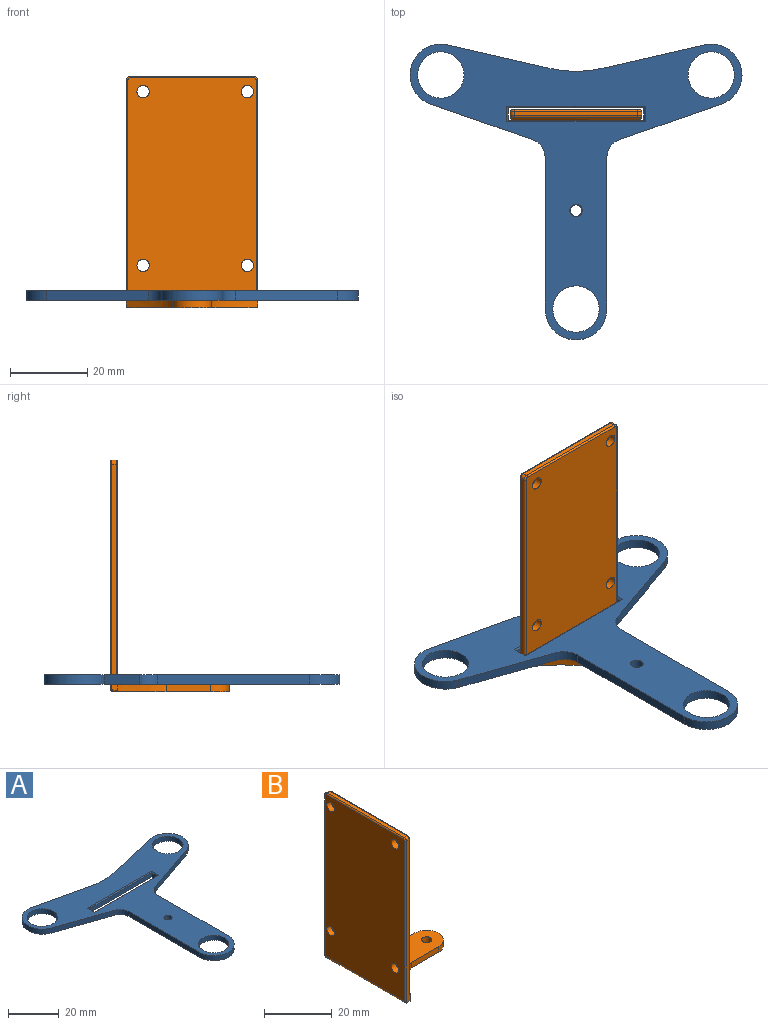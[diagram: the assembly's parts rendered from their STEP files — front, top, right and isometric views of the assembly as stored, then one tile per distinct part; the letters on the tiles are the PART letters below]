
ASSEMBLY  parts=2 mates=1
PART A: 26 faces, bbox 86x76.6x2.4 mm
  f0: plane 26.46x6.1mm, normal (0.22,0.97,0), area 65.2mm2, adj f1,f17,f18,f23
  f1: cylinder r=8mm len=15.55mm, axis (0,0,-1), area 58.2mm2, adj f0,f2,f17,f18
  f2: plane 26.29x9.18mm, normal (-0.33,-0.94,0), area 66.8mm2, adj f1,f17,f18,f24
  f3: plane 39.17x2.4mm, normal (-1,0,0), area 94mm2, adj f4,f17,f18,f24
  f4: cylinder r=8mm len=16mm, axis (0,0,-1), area 60.3mm2, adj f3,f5,f17,f18
  f5: plane 39.17x2.4mm, normal (1,0,0), area 94mm2, adj f4,f17,f18,f25
  f6: plane 26.29x9.18mm, normal (0.33,-0.94,0), area 66.8mm2, adj f7,f17,f18,f25
  f7: cylinder r=8mm len=15.55mm, axis (0,0,-1), area 58.2mm2, adj f6,f16,f17,f18
  f8: plane 3.2x2mm, normal (-1,0,0), area 6.4mm2, adj f9,f15,f18,f22
  f9: plane 35x2mm, normal (0,1,0), area 70mm2, adj f8,f10,f18,f20
  f10: plane 3.2x2mm, normal (1,0,0), area 6.4mm2, adj f9,f15,f18,f19
  f11: cylinder r=6mm len=12mm, axis (0,0,-1), area 90.5mm2, adj f17,f18
  f12: cylinder r=6mm len=12mm, axis (0,0,-1), area 90.5mm2, adj f17,f18
  f13: cylinder r=6mm len=12mm, axis (0,0,-1), area 90.5mm2, adj f17,f18
  f14: cylinder r=1.6mm len=3.2mm, axis (0,0,-1), area 24.1mm2, adj f17,f18
  f15: plane 35x2mm, normal (0,-1,0), area 70mm2, adj f8,f10,f18,f21
  f16: plane 26.47x6.1mm, normal (-0.22,0.97,0), area 65.2mm2, adj f7,f17,f18,f23
  f17: plane 86x76.62mm, normal (0,0,1), area 1794.3mm2, adj f0,f1,f2,f3,f4,f5,f6,f7
  f18: plane 86x76.62mm, normal (0,0,-1), area 1825.5mm2, adj f0,f1,f2,f3,f4,f5,f6,f7
  f19: plane 4x0.4mm, normal (0.71,0,0.71), area 2mm2, adj f10,f17,f20,f21
  f20: plane 35.8x0.4mm, normal (0,0.71,0.71), area 20mm2, adj f9,f17,f19,f22
  f21: plane 35.8x0.4mm, normal (0,-0.71,0.71), area 20mm2, adj f15,f17,f19,f22
  f22: plane 4x0.4mm, normal (-0.71,0,0.71), area 2mm2, adj f8,f17,f20,f21
  f23: cylinder r=30mm len=13.48mm, axis (0,0,-1), area 32.6mm2, adj f0,f16,f17,f18
  f24: cylinder r=5mm len=4.72mm, axis (0,0,1), area 14.8mm2, adj f2,f3,f17,f18
  f25: cylinder r=5mm len=4.72mm, axis (0,0,1), area 14.8mm2, adj f5,f6,f17,f18
PART B: 37 faces, bbox 30.9x34.2x60.2 mm
  f0: plane 58.6x1.6mm, normal (0,-1,0), area 71.2mm2, adj f1,f18,f21,f22,f23,f31,f33
  f1: extruded ~12.5x12mm, area 35.7mm2, adj f0,f2,f9,f10,f17,f21,f31
  f2: plane 11.5x2mm, normal (0,-1,0), area 23mm2, adj f1,f3,f9,f10
  f3: cylinder r=5mm len=10mm, axis (0,0,-1), area 30.6mm2, adj f2,f4,f9,f10
  f4: plane 12x2mm, normal (0,1,0), area 24mm2, adj f3,f5,f9,f10
  f5: extruded ~12x12mm, area 35.1mm2, adj f4,f6,f9,f10,f17,f29,f30
  f6: plane 58.6x1.6mm, normal (0,1,0), area 71.2mm2, adj f5,f19,f27,f28,f29,f30,f32
  f7: plane 58.6x33.2mm, normal (-1,0,0), area 1913.2mm2, adj f13,f14,f15,f16,f20,f23,f24,f25
  f8: cylinder r=1.5mm len=3mm, axis (0,0,-1), area 18.8mm2, adj f9,f10
  f9: plane 30.38x27.47mm, normal (0,0,1), area 342.9mm2, adj f1,f2,f3,f4,f5,f8,f17
  f10: plane 33.86x29.8mm, normal (0,0,-1), area 427.1mm2, adj f1,f2,f3,f4,f5,f8,f20,f21
  f11: plane 56x33.2mm, normal (1,0,0), area 1826.9mm2, adj f13,f14,f15,f16,f17,f32,f33,f34
  f12: plane 32x1.2mm, normal (0,0,1), area 38.4mm2, adj f18,f19,f25,f36
  f13: cylinder r=1.6mm len=3.2mm, axis (1,0,0), area 20.1mm2, adj f7,f11
  f14: cylinder r=1.6mm len=3.2mm, axis (1,0,0), area 20.1mm2, adj f7,f11
  f15: cylinder r=1.6mm len=3.2mm, axis (1,0,0), area 20.1mm2, adj f7,f11
  f16: cylinder r=1.6mm len=3.2mm, axis (1,0,0), area 20.1mm2, adj f7,f11
  f17: cylinder r=1.6mm len=33.2mm, axis (0,-1,0), area 81.1mm2, adj f1,f5,f9,f11,f30,f31
  f18: cylinder r=1mm len=1.2mm, axis (-1,0,0), area 1.9mm2, adj f0,f12,f24,f35
  f19: cylinder r=1mm len=1.2mm, axis (1,0,0), area 1.9mm2, adj f6,f12,f26,f34
  f20: cylinder r=1mm len=33.2mm, axis (0,-1,0), area 52.2mm2, adj f7,f10,f22,f28
  f21: cylinder r=0.4mm len=1.32mm, axis (1,0,0), area 0.7mm2, adj f0,f1,f10,f22
  f22: torus R=0.6mm, axis (0,1,0), area 0.8mm2, adj f0,f20,f21,f23
  f23: cylinder r=0.4mm len=58mm, axis (0,0,-1), area 36.4mm2, adj f0,f7,f22,f24
  f24: torus R=0.6mm, axis (1,0,0), area 0.8mm2, adj f7,f18,f23,f25
  f25: cylinder r=0.4mm len=32mm, axis (0,1,0), area 20.1mm2, adj f7,f12,f24,f26
  f26: torus R=0.6mm, axis (1,0,0), area 0.8mm2, adj f7,f19,f25,f27
  f27: cylinder r=0.4mm len=58mm, axis (0,0,1), area 36.4mm2, adj f6,f7,f26,f28
  f28: torus R=0.6mm, axis (0,1,0), area 0.8mm2, adj f6,f20,f27,f29
  f29: cylinder r=0.4mm len=1.3mm, axis (-1,0,0), area 0.7mm2, adj f5,f6,f10,f28
  f30: torus R=2mm, axis (0,1,0), area 0.6mm2, adj f5,f6,f17,f32
  f31: torus R=2mm, axis (0,1,0), area 0.6mm2, adj f0,f1,f17,f33
  f32: cylinder r=0.4mm len=55.4mm, axis (0,0,-1), area 34.8mm2, adj f6,f11,f30,f34
  f33: cylinder r=0.4mm len=55.4mm, axis (0,0,1), area 34.8mm2, adj f0,f11,f31,f35
  f34: torus R=0.6mm, axis (1,0,0), area 0.8mm2, adj f11,f19,f32,f36
  f35: torus R=0.6mm, axis (1,0,0), area 0.8mm2, adj f11,f18,f33,f36
  f36: cylinder r=0.4mm len=32mm, axis (0,-1,0), area 20.1mm2, adj f11,f12,f34,f35
PLACE A t=(-10.71,10.49,14.57)mm
PLACE B rot(axis=(0,0,-1),90deg) t=(-10.71,20.59,12.57)mm
MATE fastened B.f8 <-> A.f14  axis (0,0,1) through (-10.71,-4.41,14.57)mm
